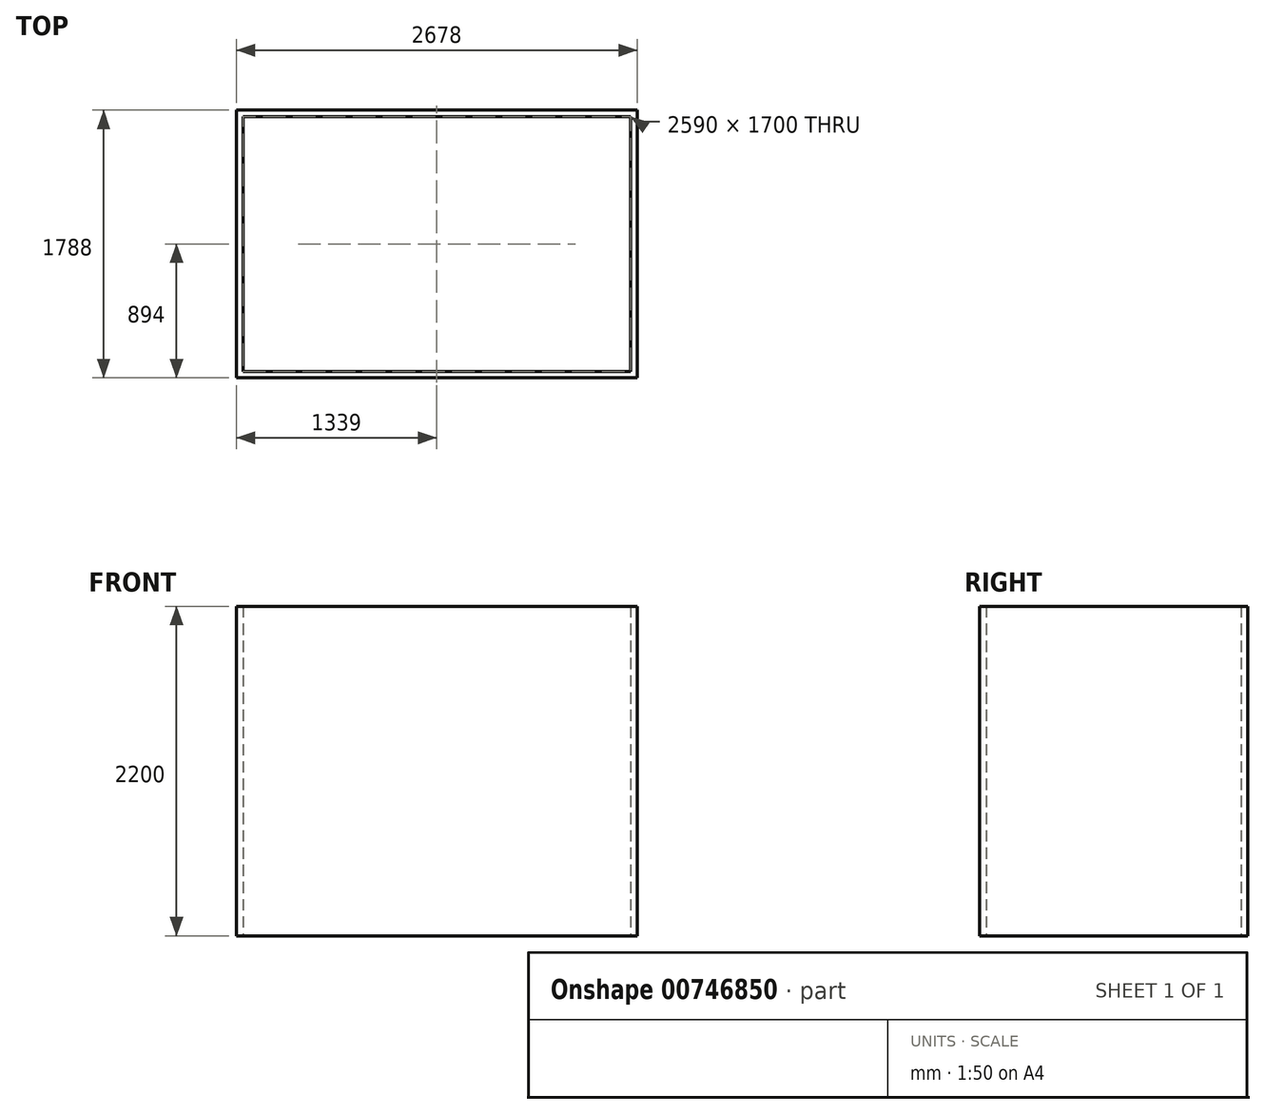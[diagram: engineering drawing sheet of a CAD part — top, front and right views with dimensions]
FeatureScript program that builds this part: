
annotation { "Feature Type Name" : "Feature", "Feature Type Description" : "" }
export const myFeature = defineFeature(function(context is Context, id is Id, definition is map)
    precondition{}
    {
        {
            var Q0;
            Q0=qCreatedBy(makeId("Top.planeOp"),FACE);
            var sketch = newSketch(context, id + "F0", { "sketchPlane" : qUnion([Q0])});
            skLineSegment(sketch, "E0.bottom", {"start": v(0, 0) * mm, "end": v(2590, 0) * mm});
            skLineSegment(sketch, "E0.top", {"start": v(0, -1700) * mm, "end": v(2590, -1700) * mm});
            skLineSegment(sketch, "E0.left", {"start": v(0, 0) * mm, "end": v(0, -1700) * mm});
            skLineSegment(sketch, "E0.right", {"start": v(2590, 0) * mm, "end": v(2590, -1700) * mm});
            skLineSegment(sketch, "E1.0", {"start": v(-44, 44) * mm, "end": v(-44, -1744) * mm});
            skLineSegment(sketch, "E1.1", {"start": v(-44, 44) * mm, "end": v(2634, 44) * mm});
            skLineSegment(sketch, "E1.2", {"start": v(2634, 44) * mm, "end": v(2634, -1744) * mm});
            skLineSegment(sketch, "E1.3", {"start": v(-44, -1744) * mm, "end": v(2634, -1744) * mm});
            skSolve(sketch);
        }
        {
            var Q0;
            Q0=makeQuery(id+"F0.imprint","IMPRINT",FACE,{"disambiguationData":[TD([[makeQuery(id+"F0.imprint","IMPRINT",EDGE,{"derivedFrom":sQuery(id+"F0.wireOp",EDGE,"E0.bottom")}),1.0]])]});
            extrude(context, id + "F1", {"entities" : qUnion([Q0]), "depth" : 2200 * mm, "offsetDistance" : 25 * mm});
        }
    });
